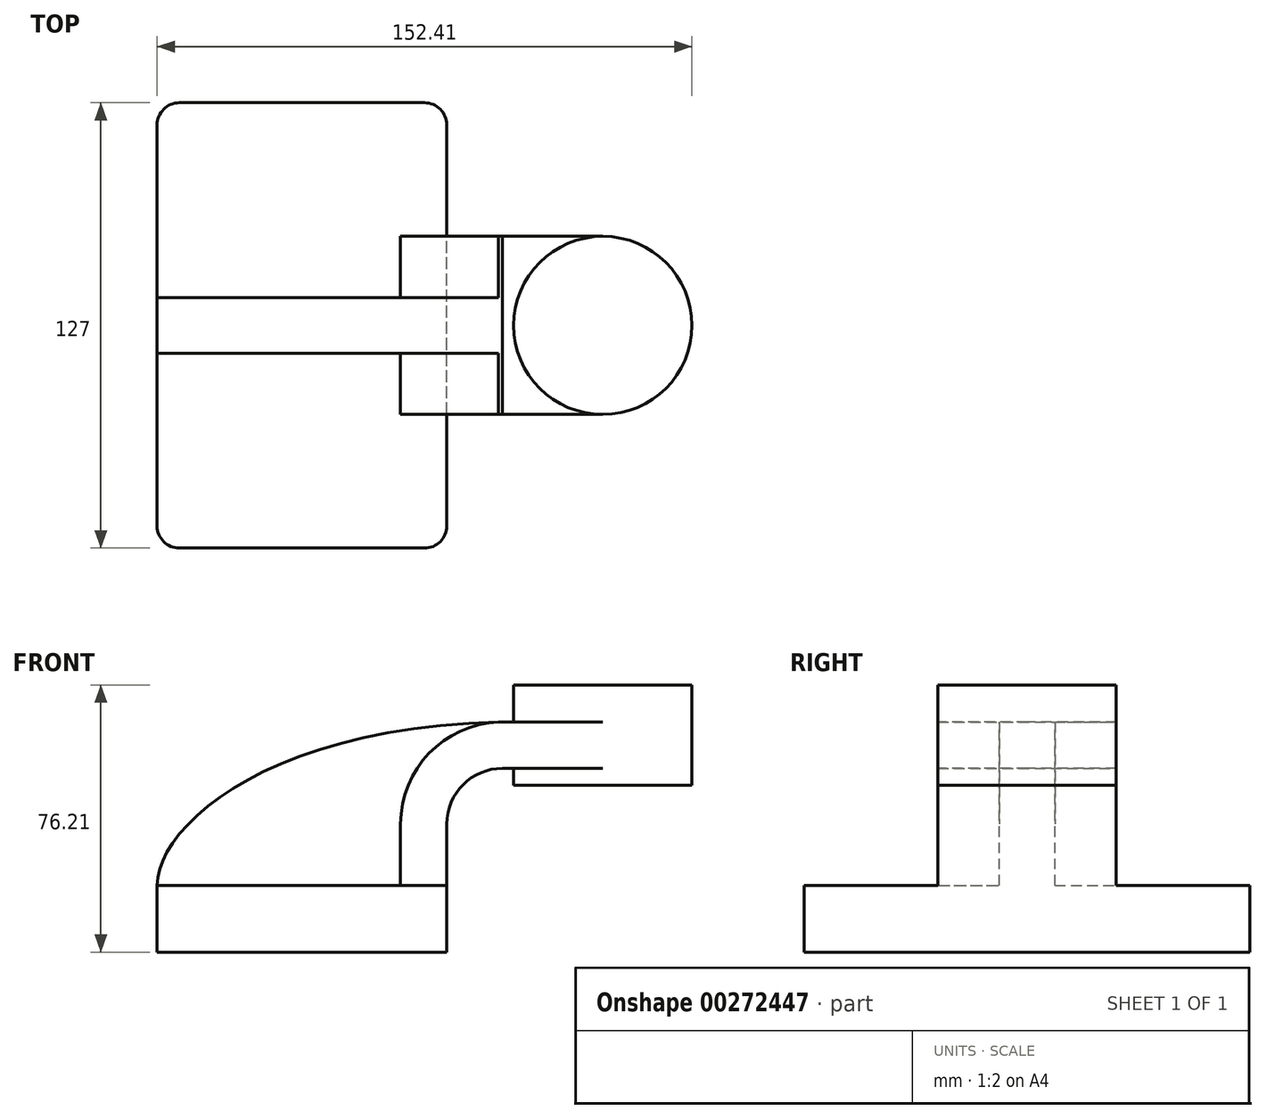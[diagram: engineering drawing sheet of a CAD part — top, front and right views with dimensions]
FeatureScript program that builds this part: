
annotation { "Feature Type Name" : "Feature", "Feature Type Description" : "" }
export const myFeature = defineFeature(function(context is Context, id is Id, definition is map)
    precondition{}
    {
        {
            var Q0;
            Q0=qCreatedBy(makeId("Front.planeOp"),FACE);
            var sketch = newSketch(context, id + "F0", { "sketchPlane" : qUnion([Q0])});
            skLineSegment(sketch, "E0.bottom", {"start": v(-41.28, 9.53) * mm, "end": v(41.27, 9.53) * mm});
            skLineSegment(sketch, "E0.top", {"start": v(-41.27, -9.52) * mm, "end": v(41.28, -9.52) * mm});
            skLineSegment(sketch, "E0.left", {"start": v(-41.27, 9.53) * mm, "end": v(-41.27, -9.52) * mm});
            skLineSegment(sketch, "E0.right", {"start": v(41.28, 9.53) * mm, "end": v(41.28, -9.52) * mm});
            skPoint(sketch, "E0.middle", {"position": v(0, 0) * mm});
            skLineSegment(sketch, "E1", {"start": v(41.27, 9.53) * mm, "end": v(41.27, 27) * mm});
            skArc(sketch, "E2", {"start": v(41.27, 27) * mm, "mid": v(45.92, 38.23) * mm, "end": v(57.15, 42.88) * mm});
            skLineSegment(sketch, "E3", {"start": v(57.15, 42.88) * mm, "end": v(85.72, 42.88) * mm});
            skLineSegment(sketch, "E4.bottom", {"start": v(111.12, 38.1) * mm, "end": v(60.32, 38.1) * mm});
            skLineSegment(sketch, "E4.top", {"start": v(111.12, 66.68) * mm, "end": v(60.32, 66.68) * mm});
            skLineSegment(sketch, "E4.left", {"start": v(111.12, 38.1) * mm, "end": v(111.12, 66.68) * mm});
            skLineSegment(sketch, "E4.right", {"start": v(60.32, 38.1) * mm, "end": v(60.32, 66.68) * mm});
            skPoint(sketch, "E4.middle", {"position": v(85.72, 52.39) * mm});
            skLineSegment(sketch, "E5.0", {"start": v(57.15, 56.06) * mm, "end": v(85.72, 56.06) * mm});
            skArc(sketch, "E5.1", {"start": v(28.1, 27) * mm, "mid": v(36.6, 47.55) * mm, "end": v(57.15, 56.06) * mm});
            skLineSegment(sketch, "E5.2", {"start": v(28.1, 9.53) * mm, "end": v(28.1, 27) * mm});
            skLineSegment(sketch, "E6", {"start": v(85.72, 38.1) * mm, "end": v(85.72, 66.68) * mm});
            skFitSpline(sketch, "E7", {"points": [v(-41.27, 9.52) * mm, v(57.15, 56.06) * mm], "startDerivative": vector(-0.04, 49.36) * mm, "endDerivative": vector(201.98, 3.44) * mm});
            skSolve(sketch);
        }
        {
            var Q0;
            Q0=makeQuery(id+"F0.imprint","IMPRINT",FACE,{"disambiguationData":[TD([[makeQuery(id+"F0.imprint","IMPRINT",EDGE,{"derivedFrom":sQuery(id+"F0.wireOp",EDGE,"E0.top")}),1.0]])]});
            extrude(context, id + "F1", {"entities" : qUnion([Q0]), "endBound" : BoundingType.SYMMETRIC, "depth" : 127 * mm});
        }
        {
            var Q0;
            {var subQ9=sQuery(id+"F0.wireOp",EDGE,"E1");Q0=makeQuery(id+"F0.imprint","IMPRINT",FACE,{"disambiguationData":[TD([[makeQuery(id+"F0.imprint","IMPRINT",EDGE,{"derivedFrom":subQ9}),1.0]])]});}
            var Q1;
            {var subQ0=sQuery(id+"F0.wireOp",EDGE,"E6");var subQ1=sQuery(id+"F0.wireOp",EDGE,"E3");var subQ2=makeQuery(id+"F0.imprint","INTERSECT",VERTEX,{"derivedFrom":[subQ1,subQ0]});Q1=makeQuery(id+"F0.imprint","IMPRINT",FACE,{"disambiguationData":[TD([[makeQuery(id+"F0.imprint","IMPRINT",EDGE,{"disambiguationData":[TD([[subQ2,1.0]])],"derivedFrom":subQ1}),1.0]])]});}
            extrude(context, id + "F2", {"entities" : qUnion([Q0, Q1]), "operationType" : NewBodyOperationType.ADD, "endBound" : BoundingType.SYMMETRIC, "depth" : 50.8 * mm});
        }
        {
            var Q0;
            {var subQ3=sQuery(id+"F0.wireOp",EDGE,"E5.2");Q0=makeQuery(id+"F0.imprint","IMPRINT",FACE,{"disambiguationData":[TD([[makeQuery(id+"F0.imprint","IMPRINT",EDGE,{"derivedFrom":subQ3}),1.0]])]});}
            extrude(context, id + "F3", {"entities" : qUnion([Q0]), "operationType" : NewBodyOperationType.ADD, "endBound" : BoundingType.SYMMETRIC, "depth" : 15.88 * mm});
        }
        {
            var Q0;
            {var subQ4=sQuery(id+"F0.wireOp",EDGE,"E4.left");Q0=makeQuery(id+"F0.imprint","IMPRINT",FACE,{"disambiguationData":[TD([[makeQuery(id+"F0.imprint","IMPRINT",EDGE,{"derivedFrom":subQ4}),1.0]])]});}
            var Q1;
            Q1=sQuery(id+"F0.wireOp",EDGE,"E6");
            revolve(context, id + "F4", {"operationType" : NewBodyOperationType.ADD, "entities" : qUnion([Q0]), "axis" : qUnion([Q1]), "revolveType" : RevolveType.FULL});
        }
        {
            var Q0;
            Q0=makeQuery(id+"F1.opExtrude","CAP_EDGE",EDGE,{"disambiguationData":[OSD([sQuery(id+"F0.wireOp",EDGE,"E0.left")])],"isStart":false});
            var Q1;
            Q1=makeQuery(id+"F1.opExtrude","CAP_EDGE",EDGE,{"disambiguationData":[OSD([sQuery(id+"F0.wireOp",EDGE,"E0.right")])],"isStart":false});
            var Q2;
            Q2=makeQuery(id+"F1.opExtrude","CAP_EDGE",EDGE,{"disambiguationData":[OSD([sQuery(id+"F0.wireOp",EDGE,"E0.left")])],"isStart":true});
            var Q3;
            Q3=makeQuery(id+"F1.opExtrude","CAP_EDGE",EDGE,{"disambiguationData":[OSD([sQuery(id+"F0.wireOp",EDGE,"E0.right")])],"isStart":true});
            fillet(context, id + "F5", {"entities" : qUnion([Q0, Q1, Q2, Q3]), "radius" : 6.35 * mm, "tangentPropagation" : true, "allowEdgeOverflow" : false});
        }
    });
